# Revit family: NEW01-ARMARIO METAL_AP12-AP22-AP32-AP45-AP52-AP56
name_source: partatom
category: Furniture
revit_build: Autodesk Revit Architecture 2014 (Build: 20130308_1515(x64)
units: mm (PartAtom-declared; Revit-internal decimal feet)

## types (6) — shared parameters
BO_Depth = 432 mm  [stored 1.41732 ft]
BO_Door MFC Maple = Maple
BO_Door MFC Walnut = Walnut
BO_Door MFC Wangue = Wangue
BO_Door MFC White = White
BO_Door Steel Black = Black
BO_Door Steel Blue = Blue
BO_Door Steel Orange = Orange
BO_Door Steel Pistache = Pistache
BO_Door Steel Silver = Steel, Paint Finish, Dark Gray, Matte
BO_Door Steel White = Steel, Paint Finish, Ivory, Glossy
BO_Handles = Steel, Paint Finish, Dark Gray, Matte
BO_Height = 1300 mm  [stored 4.26509 ft]
BO_Lock Distance = 438.5 mm  [stored 1.43865 ft]
BO_Structure Silver = Steel, Paint Finish, Dark Gray, Matte
BO_Structure White = Steel, Paint Finish, Ivory, Glossy
BO_Technical Data = http://www.actiu.com
BO_URL Model = http://www.actiu.com
BO_Width = 798 mm  [stored 2.61811 ft]
Description = Metal Storage are presented as a current and efficient solution of filing and storage.
Manufacturer = Actiu Berbegal y Formas S.A.
Model = ARMARIO METAL
URL = www.actiu.com

## per-type parameters (varying)
| type | BO_Door Handle Height | BO_Door Height | BO_Lock Height | BO_Visibility Door | BO_Visibility Door Handles | BO_Visibility Drawers 1 | BO_Visibility Drawers 2 | BO_Visibility Drawers 3 | BO_Visibility Drawers Handles 1 | BO_Visibility Drawers Handles 2 | BO_Visibility Drawers Handles 3 | BO_Visibility Drawers Handles 4 | BO_Visibility Lock 1 | BO_Visibility Lock 2 | BO_Visibility Shelf 1 | BO_Visibility Shelf 2 |
| AP12 | 843.5 mm  [stored 2.76739 ft] | 1252 mm  [stored 4.10761 ft] | 797.5 mm | No | No | No | No | No | No | No | No | No | No | No | Yes | No |
| AP22 | 843.5 mm  [stored 2.76739 ft] | 1252 mm  [stored 4.10761 ft] | 797.5 mm | Yes | Yes | No | No | No | No | No | No | No | Yes | No | Yes | No |
| AP32 | 543.5 mm  [stored 1.78314 ft] | 652 mm  [stored 2.13911 ft] | 624 mm  [stored 2.04724 ft] | Yes | Yes | No | No | No | No | No | No | No | Yes | No | No | Yes |
| AP45 | 543.5 mm  [stored 1.78314 ft] | 652 mm  [stored 2.13911 ft] | 624 mm  [stored 2.04724 ft] | No | No | Yes | No | No | Yes | No | Yes | No | No | Yes | No | Yes |
| AP52 | 543.5 mm  [stored 1.78314 ft] | 652 mm  [stored 2.13911 ft] | 624 mm  [stored 2.04724 ft] | No | No | No | Yes | No | Yes | Yes | Yes | Yes | No | Yes | No | Yes |
| AP56 | 543.5 mm  [stored 1.78314 ft] | 667 mm | 624 mm  [stored 2.04724 ft] | No | No | No | No | Yes | Yes | Yes | Yes | No | No | Yes | No | Yes |

note: column(s) folded — value = type name in every type: BO_Reference

note: [stored X ft] marks values corroborated as IEEE doubles in the binary element streams (Revit-internal decimal feet)
